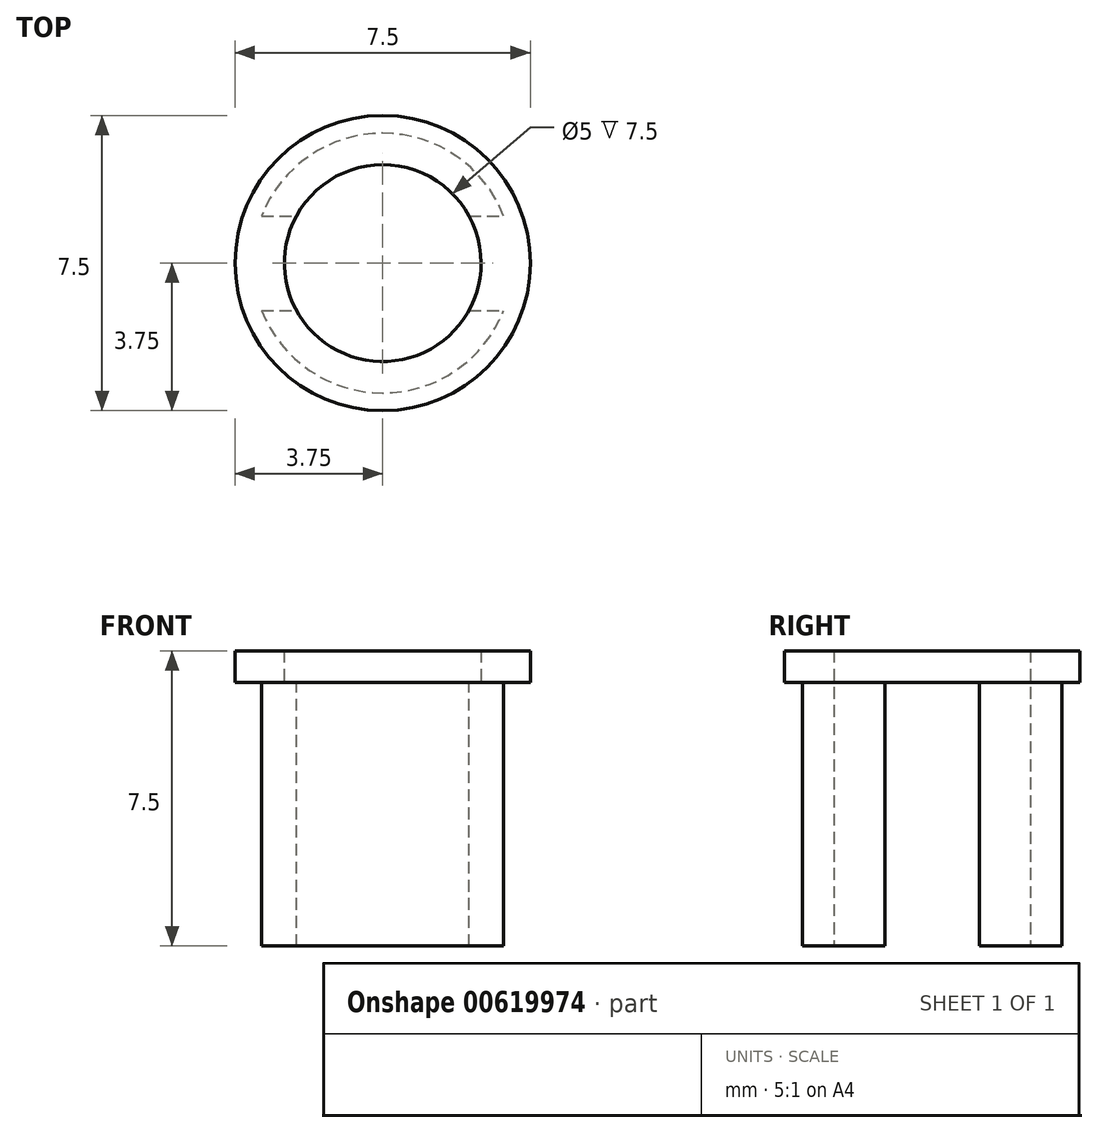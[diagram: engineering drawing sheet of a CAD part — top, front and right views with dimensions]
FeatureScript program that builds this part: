
annotation { "Feature Type Name" : "Feature", "Feature Type Description" : "" }
export const myFeature = defineFeature(function(context is Context, id is Id, definition is map)
    precondition{}
    {
        {
            var Q0;
            Q0=qCreatedBy(makeId("Top.planeOp"),FACE);
            var sketch = newSketch(context, id + "F0", { "sketchPlane" : qUnion([Q0])});
            skCircle(sketch, "E0", {"center": v(0, 0) * mm, "radius": 3.75 * mm});
            skCircle(sketch, "E1", {"center": v(0, 0) * mm, "radius": 2.5 * mm});
            skSolve(sketch);
        }
        {
            var Q0;
            Q0 = qSketchRegion(id + "F0", true);
            extrude(context, id + "F1", {"entities" : qUnion([Q0]), "depth" : 0.8 * mm, "offsetDistance" : 25 * mm});
        }
        {
            var Q0;
            Q0=makeQuery(id+"F1.opExtrude","CAP_FACE",FACE,{"disambiguationData":[OSD([sQuery(id+"F0.wireOp",EDGE,"E0"),sQuery(id+"F0.wireOp",EDGE,"E1")])],"isStart":true});
            var sketch = newSketch(context, id + "F2", { "sketchPlane" : qUnion([Q0])});
            skArc(sketch, "E2", {"start": v(-3.07, -1.2) * mm, "mid": v(0, -3.3) * mm, "end": v(3.07, -1.2) * mm});
            skArc(sketch, "E3", {"start": v(-2.2, -1.2) * mm, "mid": v(0, -2.5) * mm, "end": v(2.2, -1.2) * mm});
            skLineSegment(sketch, "E4", {"start": v(-3.07, 1.2) * mm, "end": v(-2.2, 1.2) * mm});
            skLineSegment(sketch, "E5", {"start": v(-3.07, -1.2) * mm, "end": v(-2.2, -1.2) * mm});
            skArc(sketch, "E6.trimOffspring", {"start": v(2.2, 1.2) * mm, "mid": v(0, 2.5) * mm, "end": v(-2.2, 1.2) * mm});
            skArc(sketch, "E7.trimOffspring", {"start": v(3.07, 1.2) * mm, "mid": v(0, 3.3) * mm, "end": v(-3.07, 1.2) * mm});
            skLineSegment(sketch, "E8.trimOffspring", {"start": v(2.2, -1.2) * mm, "end": v(3.07, -1.2) * mm});
            skLineSegment(sketch, "E9.trimOffspring", {"start": v(2.2, 1.2) * mm, "end": v(3.07, 1.2) * mm});
            skSolve(sketch);
        }
        {
            var Q0;
            Q0 = qSketchRegion(id + "F2", true);
            extrude(context, id + "F3", {"entities" : qUnion([Q0]), "operationType" : NewBodyOperationType.ADD, "depth" : (7.5 - 0.8) * mm, "offsetDistance" : 25 * mm});
        }
    });
